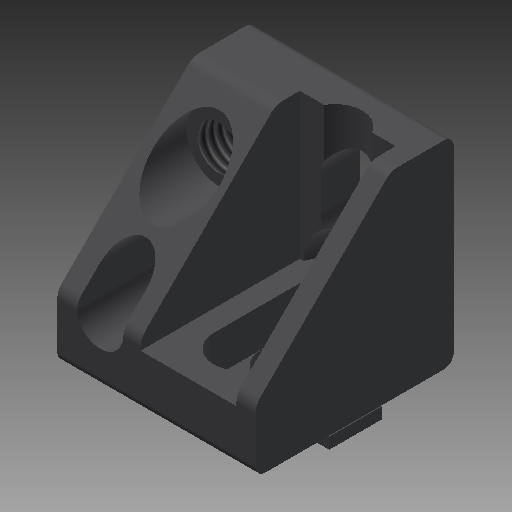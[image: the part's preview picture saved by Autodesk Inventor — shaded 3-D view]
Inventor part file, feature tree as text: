
AUTODESK INVENTOR PART (.ipt)
format: ipt  version: 2018 (Build 220112000, 112)  size: 508,416 bytes
history: native  units: mm
features: other x28, sketch x14, extrude x10, hole x3, revolve x1
ambient origin geometry x8: Origin, YZ Plane, XZ Plane, XY Plane, X Axis, Y Axis, Z Axis, Center Point
bodies: Solid1 (feature_tree)
feature tree (56):
  extrude  "Extrusion1"  Depth=30.0mm TaperAngle=0.0deg
  hole  "Drilling 1"  [1 undecoded]
  hole  "Drilling 2"  [1 undecoded]
  extrude  "Extrusion2"  Depth=17.65mm TaperAngle=0.0deg
  extrude  "Extrusion3"  Depth=8.0mm TaperAngle=0.0deg
  extrude  "Extrusion4"  [1 undecoded]
  revolve  "Revolution1"  [1 undecoded]
  extrude  "Extrusion5"  [1 undecoded]
  extrude  "Extrusion6"  [1 undecoded]
  extrude  "Extrusion7"  [1 undecoded]
  extrude  "Extrusion8"  [1 undecoded]
  extrude  "Extrusion9"  [1 undecoded]
  extrude  "Extrusion10"  [1 undecoded]
  hole  "Drilling 3"  [1 undecoded]
  other  "side_1_XY"
  other  "side_1_YZ"
  other  "side_1_ZX"
  other  "side_1_X"
  other  "side_1_Y"
  other  "side_1_Z"
  other  "side_1_Center"
  other  "side_2a_XY"
  other  "side_2a_YZ"
  other  "side_2a_ZX"
  other  "side_2a_X"
  other  "side_2a_Y"
  other  "side_2a_Z"
  other  "side_2a_Center"
  other  "side_2b_XY"
  other  "side_2b_YZ"
  other  "side_2b_ZX"
  other  "side_2b_X"
  other  "side_2b_Y"
  other  "side_2b_Z"
  other  "side_2b_Center"
  other  "side_2c_XY"
  other  "side_2c_YZ"
  other  "side_2c_ZX"
  other  "side_2c_X"
  other  "side_2c_Y"
  other  "side_2c_Z"
  other  "side_2c_Center"
  sketch  "Skizze_1"  dims[d0=30.0mm d1=0.0mm]
  sketch  "Sketch2"  dims[d9=10.0mm d10=6.0mm d11=4.0mm d12=2.0mm d13=90.0deg d14=13.0mm d15=0.0mm d16=30.0mm d17=0.0mm]
  sketch  "Sketch3"  dims[d18=24.1mm d19=0.0mm d20=30.0mm d21=0.0mm]
  sketch  "Skizze_5"  dims[d29=12.2mm d30=0.0mm d31=8.0mm d32=0.0mm]
  sketch  "Skizze_4"  dims[d22=180.0deg d23=30.0mm d24=0.0mm]
  sketch  "Skizze_6"  dims[d33=12.0mm d34=0.0mm]
  sketch  "Skizze_8"
  sketch  "Skizze_9"
  sketch  "Skizze_10"
  sketch  "Skizze_11"
  sketch  "Skizze_7"  dims[d35=8.2mm d36=6.0mm d37=4.0mm d38=2.0mm d39=90.0deg d40=4.0mm d41=0.0mm]
  sketch  "Sketch_1"  dims[d2=6.647mm d3=12.0mm d4=8.0mm d5=2.0mm d6=15.707963mm d7=12.0mm d8=0.0mm]
  sketch  "Sketch_4"  dims[d25=2.0mm d26=0.0mm d27=17.65mm d28=0.0mm]
  sketch  "Sketch14"
note: 11 required parameter values undecoded (feature->parameter linkage not recoverable at this tier; creation-order binding heuristic only, values carry confidence <= 0.55)
